# Revit family: Workstations-Multi_Level-Teknion-B_ASR_Secondary_Desk_for_Height_Adjustable_Run_Off-R2018
name_source: partatom
category: Furniture
revit_build: Autodesk Revit 2018 (Build: 20170223_1515(x64)
units: mm (PartAtom-declared; Revit-internal decimal feet)

## family parameters
Always vertical = Yes
Cut with Voids When Loaded = No
OmniClass Number = 23.40.20.00
OmniClass Title = General Furniture and Specialties
Room Calculation Point = No
Shared = Yes
Work Plane-Based = No

## types (6) — shared parameters
Assembly Code = E2020200
Manufacturer = Teknion
Manufacturer Fax = 416.661.4586
Part Number = B_ASR
Product Documentation Link = https://www.teknion.com
Product Line = Expansion Casegoods
Product Page URL = https://www.teknion.com
Series = Expansion Casegoods
Sustainability Data = https://www.teknion.com
URL = www.teknion.com
Unit Weight URL = http://www.teknion.com
Warranty = http://www.teknion.com

## per-type parameters (varying)
| type | Depth | Description | Height-Adjustable Worksurface Depth | Model |
| 20" Depth, 23" Height-Adjustable Worksurface Depth | 19.902 " | Secondary Desk for Height-Adjustable Run-Off and L-Shape Desk, 20" Depth, 23" Height-Adjustable Worksurface Depth | 11.941 " | B_ASR_2320_____ |
| 20" Depth, 29" Height-Adjustable Worksurface Depth | 19.902 " | Secondary Desk for Height-Adjustable Run-Off and L-Shape Desk, 20" Depth, 29" Height-Adjustable Worksurface Depth | 14.925 " | B_ASR_2920_____ |
| 20" Depth, 35" Height-Adjustable Worksurface Depth | 19.902 " | Secondary Desk for Height-Adjustable Run-Off and L-Shape Desk, 20" Depth, 35" Height-Adjustable Worksurface Depth | 17.909 " | B_ASR_3520_____ |
| 24" Depth, 35" Height-Adjustable Worksurface Depth | 23.882 " | Secondary Desk for Height-Adjustable Run-Off and L-Shape Desk, 24" Depth, 35" Height-Adjustable Worksurface Depth | 17.909 " | B_ASR_3524_____ |
| 24" Depth, 29" Height-Adjustable Worksurface Depth | 23.882 " | Secondary Desk for Height-Adjustable Run-Off and L-Shape Desk, 24" Depth, 29" Height-Adjustable Worksurface Depth | 14.925 " | B_ASR_2924_____ |
| 24" Depth, 23" Height-Adjustable Worksurface Depth | 23.882 " | Secondary Desk for Height-Adjustable Run-Off and L-Shape Desk, 24" Depth, 23" Height-Adjustable Worksurface Depth | 11.941 " | B_ASR_2324_____ |

## geometry (parser evidence)
native form markers: Sweep x3
no freeform markers — native parametric forms only
